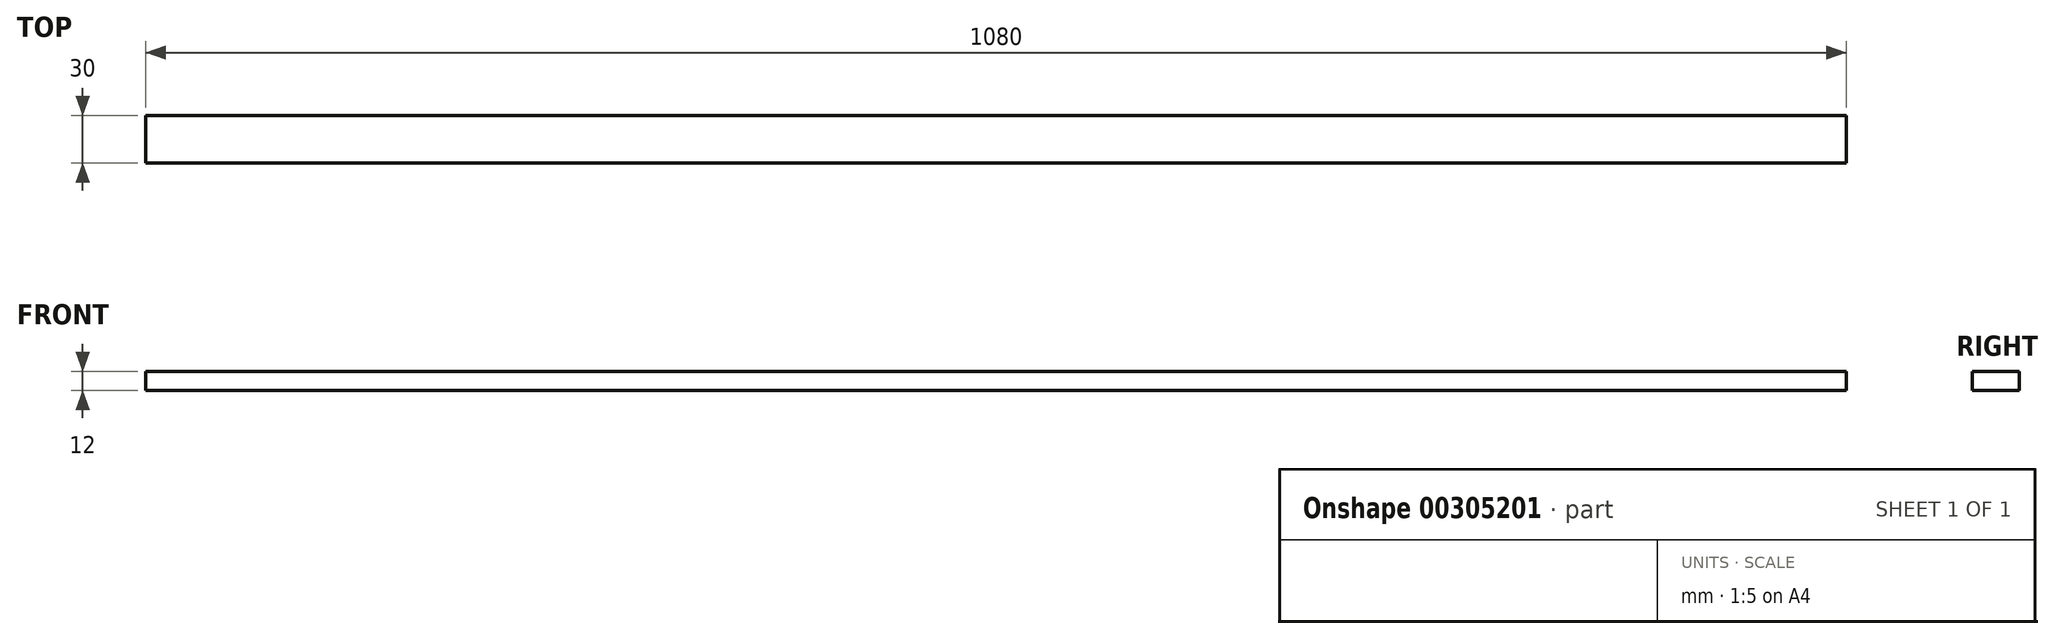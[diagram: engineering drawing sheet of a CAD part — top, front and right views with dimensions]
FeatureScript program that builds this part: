
annotation { "Feature Type Name" : "Feature", "Feature Type Description" : "" }
export const myFeature = defineFeature(function(context is Context, id is Id, definition is map)
    precondition{}
    {
        {
            var Q0;
            Q0=qCreatedBy(makeId("Top.planeOp"),FACE);
            var sketch = newSketch(context, id + "F0", { "sketchPlane" : qUnion([Q0])});
            skLineSegment(sketch, "E0.bottom", {"start": v(0, 0) * mm, "end": v(1080, 0) * mm});
            skLineSegment(sketch, "E0.top", {"start": v(0, 30) * mm, "end": v(1080, 30) * mm});
            skLineSegment(sketch, "E0.left", {"start": v(0, 0) * mm, "end": v(0, 30) * mm});
            skLineSegment(sketch, "E0.right", {"start": v(1080, 0) * mm, "end": v(1080, 30) * mm});
            skSolve(sketch);
        }
        {
            var Q0;
            Q0=makeQuery(id+"F0.imprint","IMPRINT",FACE,{"disambiguationData":[TD([[makeQuery(id+"F0.imprint","IMPRINT",EDGE,{"derivedFrom":sQuery(id+"F0.wireOp",EDGE,"E0.bottom")}),1.0]])]});
            extrude(context, id + "F1", {"entities" : qUnion([Q0]), "depth" : 12 * mm});
        }
    });
